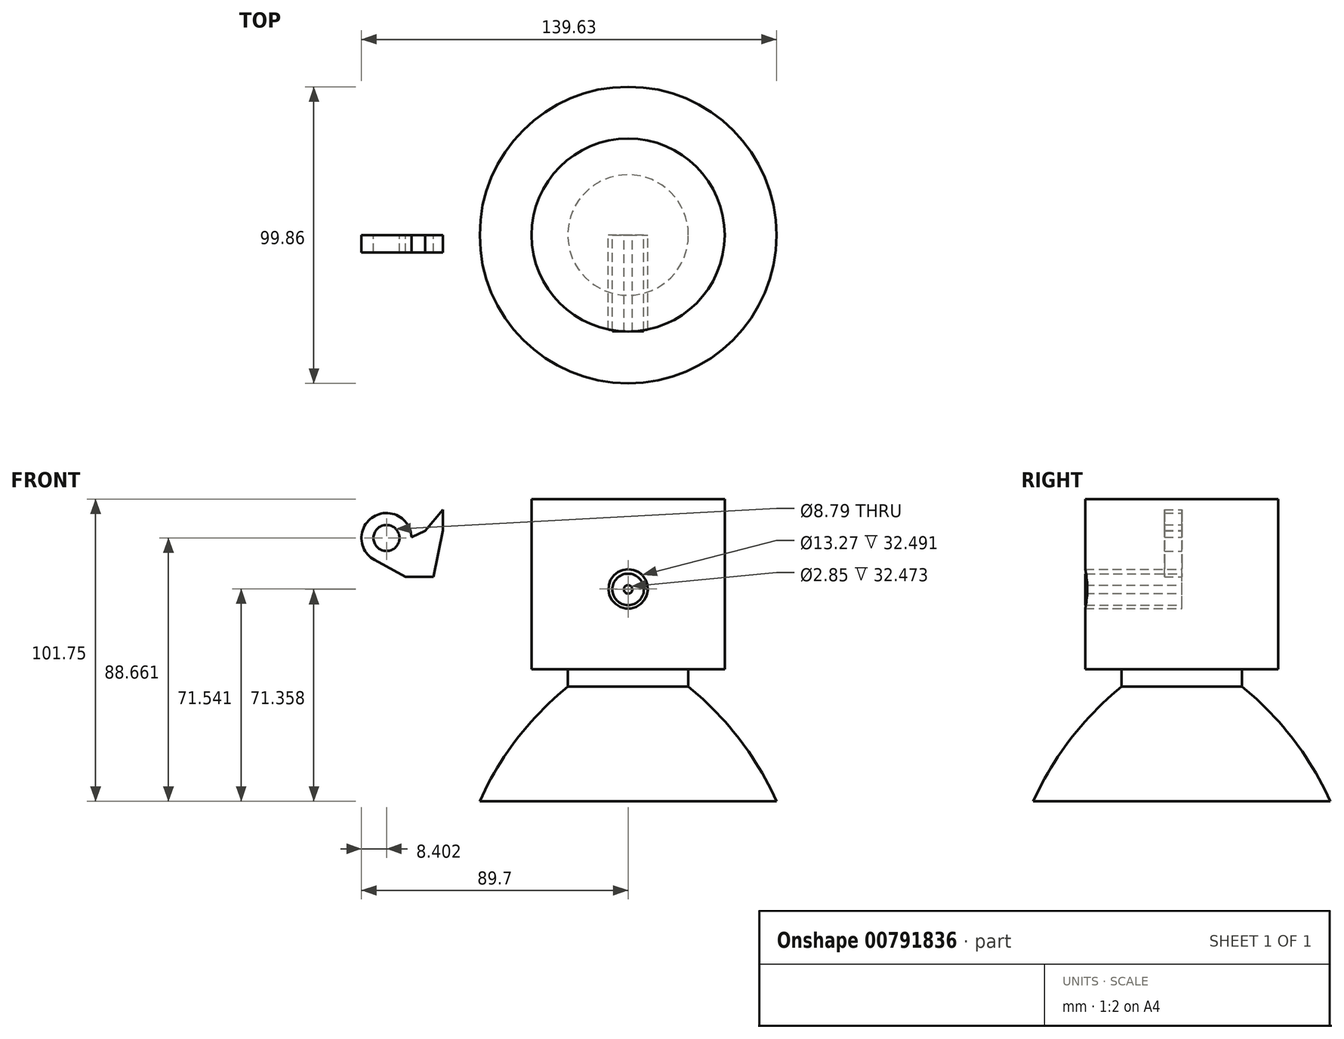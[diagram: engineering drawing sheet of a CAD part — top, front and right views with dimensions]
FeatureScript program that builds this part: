
annotation { "Feature Type Name" : "Feature", "Feature Type Description" : "" }
export const myFeature = defineFeature(function(context is Context, id is Id, definition is map)
    precondition{}
    {
        {
            var Q0;
            Q0=qCreatedBy(makeId("Top.planeOp"),FACE);
            var sketch = newSketch(context, id + "F0", { "sketchPlane" : qUnion([Q0])});
            skCircle(sketch, "E0", {"center": v(0, 0) * mm, "radius": 32.49 * mm});
            skSolve(sketch);
        }
        {
            var Q0;
            Q0 = qSketchRegion(id + "F0", true);
            extrude(context, id + "F1", {"entities" : qUnion([Q0]), "depth" : 57.28 * mm, "offsetDistance" : 25.4 * mm});
        }
        {
            var Q0;
            Q0=qCreatedBy(makeId("Front.planeOp"),FACE);
            var sketch = newSketch(context, id + "F2", { "sketchPlane" : qUnion([Q0])});
            skCircle(sketch, "E1", {"center": v(0, 27.07) * mm, "radius": 6.63 * mm});
            skSolve(sketch);
        }
        {
            var Q0;
            Q0=makeQuery(id+"F2.imprint","IMPRINT",FACE,{"disambiguationData":[TD([[makeQuery(id+"F2.imprint","IMPRINT",EDGE,{"derivedFrom":sQuery(id+"F2.wireOp",EDGE,"E1")}),1.0]])]});
            extrude(context, id + "F3", {"entities" : qUnion([Q0]), "operationType" : NewBodyOperationType.REMOVE, "depth" : 67.93 * mm, "offsetDistance" : 25.4 * mm});
        }
        {
            var Q0;
            Q0=qCreatedBy(makeId("Front.planeOp"),FACE);
            var sketch = newSketch(context, id + "F4", { "sketchPlane" : qUnion([Q0])});
            skCircle(sketch, "E2", {"center": v(0, 26.9) * mm, "radius": 5.3 * mm});
            skSolve(sketch);
        }
        {
            var Q0;
            Q0=makeQuery(id+"F4.imprint","IMPRINT",FACE,{"disambiguationData":[TD([[makeQuery(id+"F4.imprint","IMPRINT",EDGE,{"derivedFrom":sQuery(id+"F4.wireOp",EDGE,"E2")}),1.0]])]});
            extrude(context, id + "F5", {"entities" : qUnion([Q0]), "operationType" : NewBodyOperationType.ADD, "depth" : 32.47 * mm, "offsetDistance" : 25.4 * mm});
        }
        {
            var Q0;
            Q0=qCreatedBy(makeId("Front.planeOp"),FACE);
            var sketch = newSketch(context, id + "F6", { "sketchPlane" : qUnion([Q0])});
            skCircle(sketch, "E3", {"center": v(0, 26.89) * mm, "radius": 1.42 * mm});
            skSolve(sketch);
        }
        {
            var Q0;
            Q0=makeQuery(id+"F6.imprint","IMPRINT",FACE,{"disambiguationData":[TD([[makeQuery(id+"F6.imprint","IMPRINT",EDGE,{"derivedFrom":sQuery(id+"F6.wireOp",EDGE,"E3")}),1.0]])]});
            extrude(context, id + "F7", {"entities" : qUnion([Q0]), "operationType" : NewBodyOperationType.REMOVE, "depth" : 36.74 * mm, "offsetDistance" : 25.4 * mm});
        }
        {
            var Q0;
            Q0=qCreatedBy(makeId("Front.planeOp"),FACE);
            var sketch = newSketch(context, id + "F8", { "sketchPlane" : qUnion([Q0])});
            skLineSegment(sketch, "E4", {"start": v(-20.3, 0) * mm, "end": v(-20.3, -5.9) * mm});
            skLineSegment(sketch, "E5", {"start": v(-20.3, -5.9) * mm, "end": v(0, -5.9) * mm});
            skLineSegment(sketch, "E6", {"start": v(0, -5.9) * mm, "end": v(0, 0) * mm});
            skLineSegment(sketch, "E7", {"start": v(0, 0) * mm, "end": v(0, -44.47) * mm});
            skLineSegment(sketch, "E8", {"start": v(0, -44.47) * mm, "end": v(-41.01, -44.47) * mm});
            skLineSegment(sketch, "E9", {"start": v(-41.01, -44.47) * mm, "end": v(-49.93, -44.47) * mm});
            skLineSegment(sketch, "E10", {"start": v(-49.93, -44.47) * mm, "end": v(-20.3, -5.9) * mm});
            skArc(sketch, "E11", {"start": v(-20.3, -5.9) * mm, "mid": v(-37.39, -23.43) * mm, "end": v(-49.93, -44.47) * mm});
            skLineSegment(sketch, "E12", {"start": v(-20.3, 0) * mm, "end": v(0, 0) * mm});
            skLineSegment(sketch, "E13", {"start": v(0, 0) * mm, "end": v(-20.3, 0) * mm});
            skSolve(sketch);
        }
        {
            var Q0;
            Q0=makeQuery(id+"F8.imprint","IMPRINT",FACE,{"disambiguationData":[TD([[makeQuery(id+"F8.imprint","IMPRINT",EDGE,{"derivedFrom":sQuery(id+"F8.wireOp",EDGE,"E4")}),1.0]])]});
            var Q1;
            Q1=makeQuery(id+"F8.imprint","IMPRINT",FACE,{"disambiguationData":[TD([[makeQuery(id+"F8.imprint","IMPRINT",EDGE,{"derivedFrom":sQuery(id+"F8.wireOp",EDGE,"E5")}),-1.0]])]});
            var Q2;
            Q2=makeQuery(id+"F8.imprint","IMPRINT",FACE,{"disambiguationData":[TD([[makeQuery(id+"F8.imprint","IMPRINT",EDGE,{"derivedFrom":sQuery(id+"F8.wireOp",EDGE,"E10")}),1.0]])]});
            var Q3;
            Q3=sQuery(id+"F8.wireOp",EDGE,"E7");
            revolve(context, id + "F9", {"operationType" : NewBodyOperationType.ADD, "surfaceOperationType" : NewSurfaceOperationType.NEW, "entities" : qUnion([Q0, Q1, Q2]), "axis" : qUnion([Q3]), "revolveType" : RevolveType.FULL});
        }
        {
            var Q0;
            Q0=qCreatedBy(makeId("Front.planeOp"),FACE);
            var sketch = newSketch(context, id + "F10", { "sketchPlane" : qUnion([Q0])});
            skCircle(sketch, "E14", {"center": v(-81.3, 44.2) * mm, "radius": 8.4 * mm});
            skLineSegment(sketch, "E15", {"start": v(-85.3, 36.8) * mm, "end": v(-74.87, 31.17) * mm});
            skLineSegment(sketch, "E16", {"start": v(-74.87, 31.17) * mm, "end": v(-65.48, 31.17) * mm});
            skLineSegment(sketch, "E17", {"start": v(-65.48, 31.17) * mm, "end": v(-62.3, 46.77) * mm});
            skLineSegment(sketch, "E18", {"start": v(-62.3, 46.77) * mm, "end": v(-62.3, 53.68) * mm});
            skLineSegment(sketch, "E19", {"start": v(-62.3, 53.68) * mm, "end": v(-68.31, 46.55) * mm});
            skLineSegment(sketch, "E20", {"start": v(-68.31, 46.55) * mm, "end": v(-72.9, 44.46) * mm});
            skCircle(sketch, "E21", {"center": v(-81.3, 44.2) * mm, "radius": 4.4 * mm});
            skSolve(sketch);
        }
        {
            var Q0;
            Q0=makeQuery(id+"F10.imprint","IMPRINT",FACE,{"disambiguationData":[TD([[makeQuery(id+"F10.imprint","IMPRINT",EDGE,{"derivedFrom":sQuery(id+"F10.wireOp",EDGE,"E21")}),-1.0]])]});
            var Q1;
            {var subQ0=sQuery(id+"F10.wireOp",EDGE,"E15");Q1=makeQuery(id+"F10.imprint","IMPRINT",FACE,{"disambiguationData":[TD([[makeQuery(id+"F10.imprint","IMPRINT",EDGE,{"derivedFrom":subQ0}),1.0]])]});}
            extrude(context, id + "F11", {"entities" : qUnion([Q0, Q1]), "depth" : 5.84 * mm, "offsetDistance" : 25.4 * mm});
        }
    });
